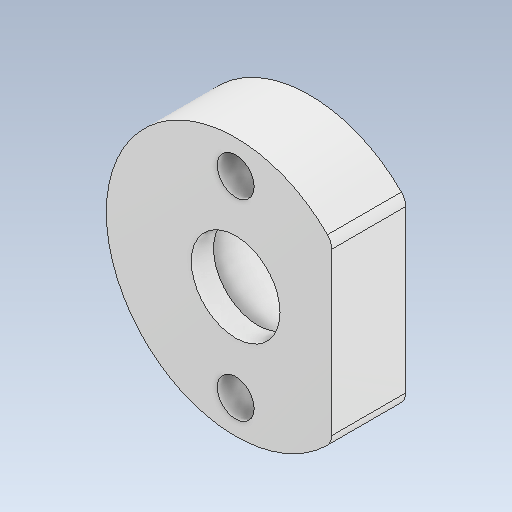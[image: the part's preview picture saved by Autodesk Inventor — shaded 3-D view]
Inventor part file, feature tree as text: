
AUTODESK INVENTOR PART (.ipt)
format: ipt  version: 2020 (Build 240168000, 168)  size: 140,288 bytes
history: native  units: mm
features: sketch x4, extrude x3, hole x1, fillet x1
ambient origin geometry x8: Origin, YZ Plane, XZ Plane, XY Plane, X Axis, Y Axis, Z Axis, Center Point
bodies: Solid1 (feature_tree)
feature tree (9):
  extrude  "Extrusion1"  Depth=35.0mm
  hole  "Hole1"  [1 undecoded]
  extrude  "Extrusion3"  Depth=2.0mm
  extrude  "Extrusion4"  TaperAngle=0.0deg  [1 undecoded]
  fillet  "Fillet2"  Radius=13.0mm
  sketch  "Sketch1"  dims[d0=12.0mm d1=35.0mm]
  sketch  "Sketch4"  dims[d2=10.0mm d3=0.0mm d7=26.0mm]
  sketch  "Sketch5"  dims[d8=5.0mm d9=6.0mm d10=4.0mm d11=2.0mm d12=90.0deg d13=8.0mm d14=20.594885mm d15=16.3mm]
  sketch  "Sketch6"  dims[d16=7.0mm d17=0.0mm d19=0.0mm d20=0.0mm d22=13.0mm d23=2.0mm]
note: 2 required parameter values undecoded (feature->parameter linkage not recoverable at this tier; creation-order binding heuristic only, values carry confidence <= 0.55)
